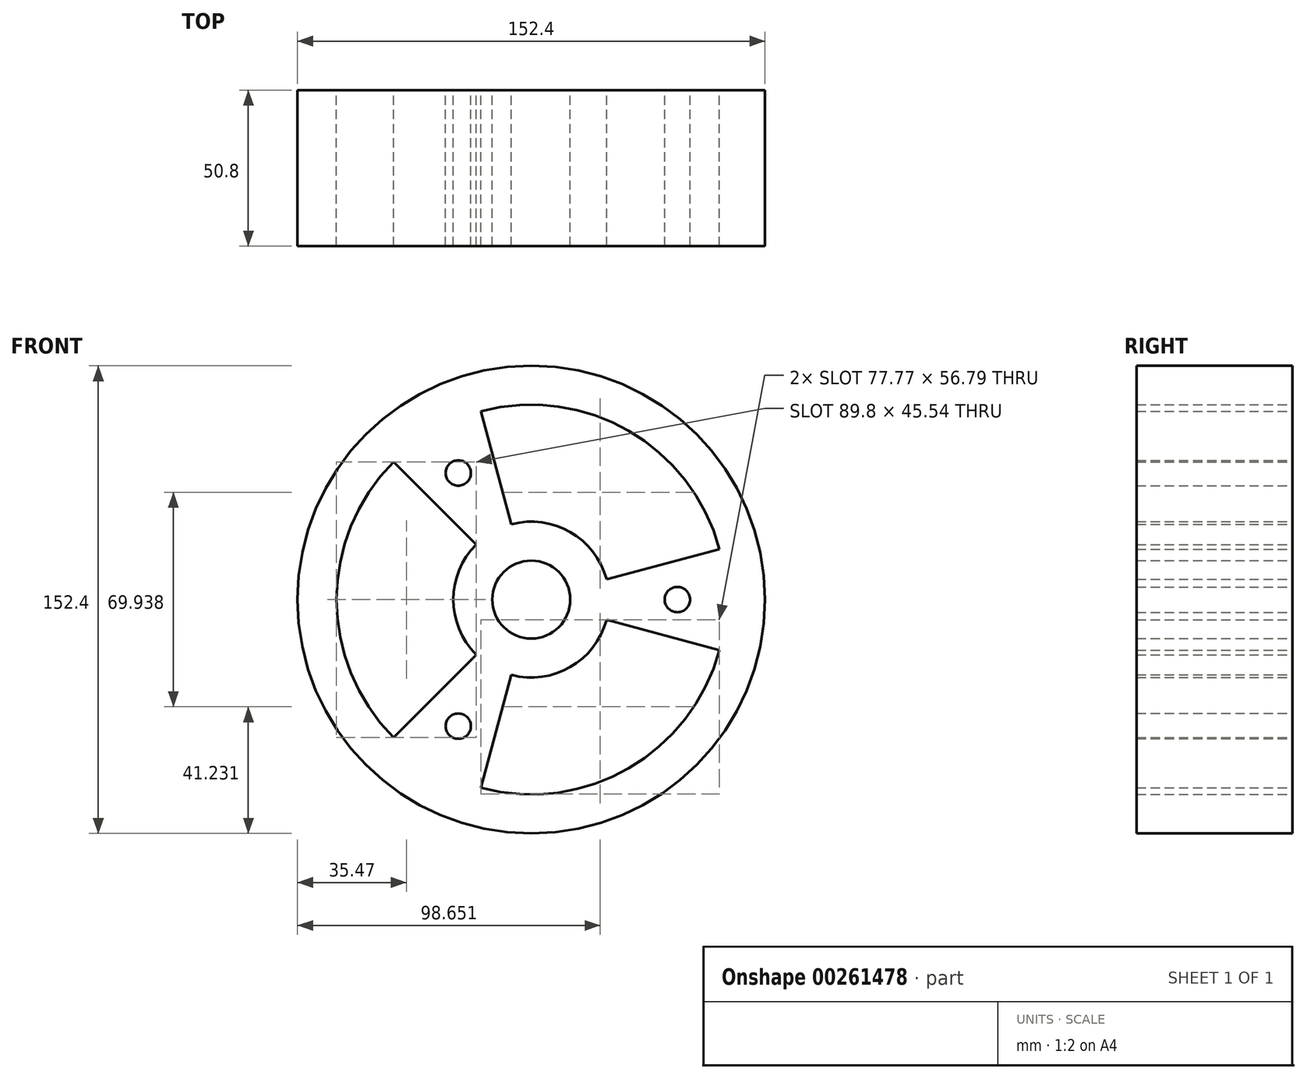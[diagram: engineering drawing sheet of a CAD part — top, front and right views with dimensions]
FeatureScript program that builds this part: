
annotation { "Feature Type Name" : "Feature", "Feature Type Description" : "" }
export const myFeature = defineFeature(function(context is Context, id is Id, definition is map)
    precondition{}
    {
        {
            var Q0;
            Q0=qCreatedBy(makeId("Front.planeOp"),FACE);
            var sketch = newSketch(context, id + "F0", { "sketchPlane" : qUnion([Q0])});
            skPoint(sketch, "E0.first.point", {"position": v(47.63, 0) * mm});
            skCircle(sketch, "E1", {"center": v(0, 0) * mm, "radius": 76.2 * mm});
            skCircle(sketch, "E2", {"center": v(0, 0) * mm, "radius": 12.7 * mm});
            skArc(sketch, "E3.0", {"start": v(-44.9, 44.9) * mm, "mid": v(-63.5, 0) * mm, "end": v(-44.9, -44.9) * mm});
            skArc(sketch, "E4.0", {"start": v(-17.96, 17.96) * mm, "mid": v(-25.4, 0) * mm, "end": v(-17.96, -17.96) * mm});
            skLineSegment(sketch, "E5", {"start": v(0.65, -12.68) * mm, "end": v(0.65, -12.68) * mm});
            skLineSegment(sketch, "E6", {"start": v(61.34, -16.44) * mm, "end": v(24.53, -6.57) * mm});
            skLineSegment(sketch, "E7", {"start": v(24.53, 6.57) * mm, "end": v(73.6, 19.72) * mm});
            skLineSegment(sketch, "E8", {"start": v(0, 0) * mm, "end": v(86.04, 0) * mm, "construction": true});
            skLineSegment(sketch, "E9.1.0", {"start": v(-16.44, 61.34) * mm, "end": v(-6.57, 24.53) * mm});
            skPoint(sketch, "E9.1.1", {"position": v(-23.81, 41.24) * mm});
            skLineSegment(sketch, "E9.1.2", {"start": v(-17.96, 17.96) * mm, "end": v(-44.9, 44.9) * mm});
            skLineSegment(sketch, "E9.2.0", {"start": v(-44.9, -44.9) * mm, "end": v(-17.96, -17.96) * mm});
            skPoint(sketch, "E9.2.1", {"position": v(-23.81, -41.24) * mm});
            skLineSegment(sketch, "E9.2.2", {"start": v(-6.57, -24.53) * mm, "end": v(-16.44, -61.34) * mm});
            skPoint(sketch, "E10.orphan", {"position": v(-19.72, 73.6) * mm});
            skPoint(sketch, "E11.orphan", {"position": v(-53.88, 53.88) * mm});
            skPoint(sketch, "E12.orphan", {"position": v(-53.88, -53.88) * mm});
            skArc(sketch, "E13.trimOffspring", {"start": v(-16.44, -61.34) * mm, "mid": v(31.75, -55) * mm, "end": v(61.34, -16.44) * mm});
            skPoint(sketch, "E14.orphan", {"position": v(-19.72, -73.6) * mm});
            skPoint(sketch, "E15.orphan", {"position": v(73.6, -19.72) * mm});
            skArc(sketch, "E16.trimOffspring", {"start": v(61.34, 16.44) * mm, "mid": v(31.75, 55) * mm, "end": v(-16.44, 61.34) * mm});
            skArc(sketch, "E17.trimOffspring", {"start": v(-6.57, -24.53) * mm, "mid": v(12.7, -22) * mm, "end": v(24.53, -6.57) * mm});
            skArc(sketch, "E18.trimOffspring", {"start": v(24.53, 6.57) * mm, "mid": v(12.7, 22) * mm, "end": v(-6.57, 24.53) * mm});
            skSolve(sketch);
        }
        {
            var Q0;
            Q0=makeQuery(id+"F0.imprint","IMPRINT",FACE,{"disambiguationData":[TD([[makeQuery(id+"F0.imprint","IMPRINT",EDGE,{"derivedFrom":sQuery(id+"F0.wireOp",EDGE,"E1")}),1.0]])]});
            extrude(context, id + "F1", {"entities" : qUnion([Q0]), "depth" : 50.8 * mm});
        }
        {
            var Q0;
            Q0=sQuery(id+"F0.wireOp",VERTEX,"E0.first.point");
            var Q1;
            Q1=sQuery(id+"F0.wireOp",VERTEX,"E9.2.1");
            var Q2;
            Q2=sQuery(id+"F0.wireOp",VERTEX,"E9.1.1");
            var Q3;
            Q3=makeQuery(id+"F1.opExtrude","SWEPT_BODY",BODY,{"disambiguationData":[OSD([sQuery(id+"F0.wireOp",EDGE,"E1"),sQuery(id+"F0.wireOp",EDGE,"E2"),sQuery(id+"F0.wireOp",EDGE,"E3.0"),sQuery(id+"F0.wireOp",EDGE,"E4.0"),sQuery(id+"F0.wireOp",EDGE,"E6"),sQuery(id+"F0.wireOp",EDGE,"E7"),sQuery(id+"F0.wireOp",EDGE,"E9.1.0"),sQuery(id+"F0.wireOp",EDGE,"E9.1.2"),sQuery(id+"F0.wireOp",EDGE,"E9.2.0"),sQuery(id+"F0.wireOp",EDGE,"E9.2.2"),sQuery(id+"F0.wireOp",EDGE,"E13.trimOffspring"),sQuery(id+"F0.wireOp",EDGE,"E16.trimOffspring"),sQuery(id+"F0.wireOp",EDGE,"E17.trimOffspring"),sQuery(id+"F0.wireOp",EDGE,"E18.trimOffspring")])]});
            hole(context, id + "F2", {"style" : HoleStyle.SIMPLE, "endStyle" : HoleEndStyle.THROUGH, "oppositeDirection" : true, "holeDiameter" : 8.25 * mm, "tappedDepth" : 12.7 * mm, "tapClearance" : 3, "locations" : qUnion([Q0, Q1, Q2]), "scope" : qUnion([Q3])});
        }
    });
